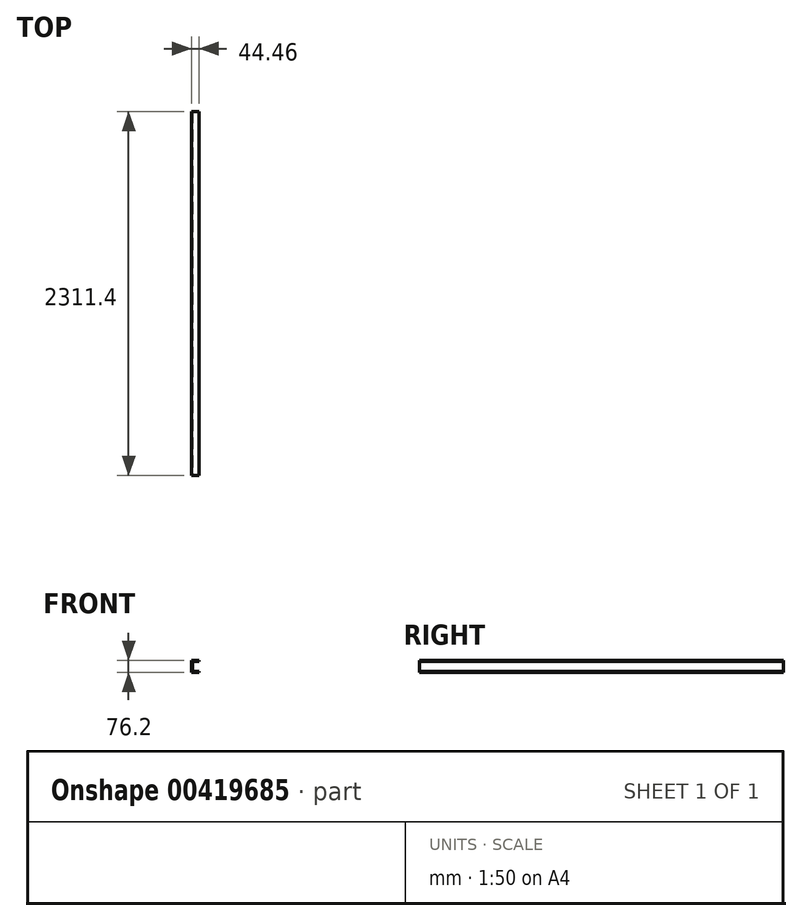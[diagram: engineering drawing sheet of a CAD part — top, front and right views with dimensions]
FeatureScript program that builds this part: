
annotation { "Feature Type Name" : "Feature", "Feature Type Description" : "" }
export const myFeature = defineFeature(function(context is Context, id is Id, definition is map)
    precondition{}
    {
        {
            var Q0;
            Q0=qCreatedBy(makeId("Front.planeOp"),FACE);
            var sketch = newSketch(context, id + "F0", { "sketchPlane" : qUnion([Q0])});
            skLineSegment(sketch, "E0.bottom", {"start": v(22.23, -38.1) * mm, "end": v(-22.23, -38.1) * mm});
            skLineSegment(sketch, "E0.top", {"start": v(22.23, 38.1) * mm, "end": v(-22.22, 38.1) * mm});
            skLineSegment(sketch, "E0.left", {"start": v(22.23, -38.1) * mm, "end": v(22.23, -31.5) * mm});
            skLineSegment(sketch, "E0.right", {"start": v(-22.23, -38.1) * mm, "end": v(-22.22, 38.1) * mm});
            skPoint(sketch, "E0.middle", {"position": v(0, 0) * mm});
            skLineSegment(sketch, "E1.0", {"start": v(-17.9, -25.15) * mm, "end": v(-17.9, 25.15) * mm});
            skLineSegment(sketch, "E2.0", {"start": v(22.23, -31.5) * mm, "end": v(-11.56, -31.5) * mm});
            skLineSegment(sketch, "E3.0", {"start": v(22.23, 31.5) * mm, "end": v(-11.56, 31.5) * mm});
            skLineSegment(sketch, "E4.trimOffspring", {"start": v(22.23, 31.5) * mm, "end": v(22.23, 38.1) * mm});
            skPoint(sketch, "E5.visualSharp", {"position": v(-17.9, 31.5) * mm});
            skArc(sketch, "E5.filletArc", {"start": v(-11.56, 31.5) * mm, "mid": v(-16.05, 29.64) * mm, "end": v(-17.9, 25.15) * mm});
            skPoint(sketch, "E6.visualSharp", {"position": v(-17.9, -31.5) * mm});
            skArc(sketch, "E6.filletArc", {"start": v(-17.9, -25.15) * mm, "mid": v(-16.05, -29.64) * mm, "end": v(-11.56, -31.5) * mm});
            skSolve(sketch);
        }
        {
            var Q0;
            Q0=makeQuery(id+"F0.imprint","IMPRINT",FACE,{"disambiguationData":[TD([[makeQuery(id+"F0.imprint","IMPRINT",EDGE,{"derivedFrom":sQuery(id+"F0.wireOp",EDGE,"E0.bottom")}),-1.0]])]});
            extrude(context, id + "F1", {"entities" : qUnion([Q0]), "oppositeDirection" : true, "depth" : 2311.4 * mm});
        }
    });
